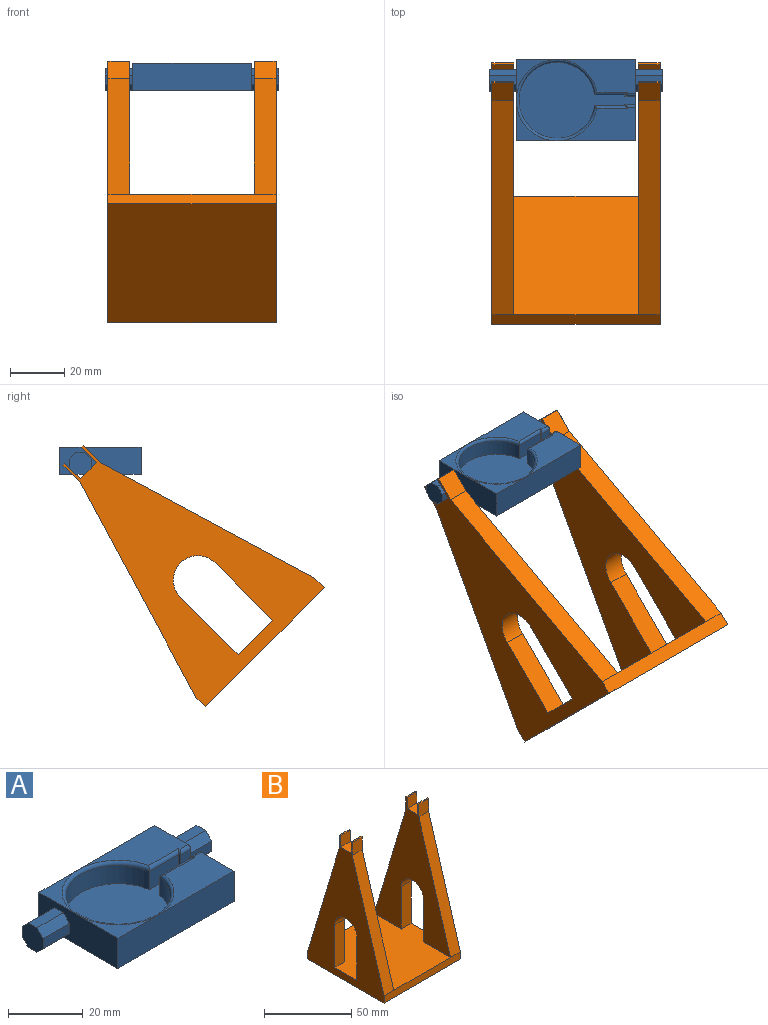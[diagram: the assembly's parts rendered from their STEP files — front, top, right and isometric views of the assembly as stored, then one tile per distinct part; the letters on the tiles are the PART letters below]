
ASSEMBLY  parts=2 mates=1
PART A: 40 faces, bbox 64x34x10 mm
  f0: plane 29x12.41mm, normal (0,0,1), area 217.2mm2, adj f3,f7,f33,f34,f35,f36
  f1: plane 29x12.59mm, normal (0,0,1), area 217.7mm2, adj f3,f6,f36,f37,f38,f39
  f2: plane 15x15mm, normal (0,0,1), area 48.3mm2, adj f4,f7,f36
  f3: plane 30x10mm, normal (1,0,0), area 225.6mm2, adj f0,f1,f6,f7,f8,f12,f13,f16
  f4: plane 30x10mm, normal (-1,0,0), area 247mm2, adj f2,f5,f6,f7,f8,f17,f18,f19
  f5: plane 15x15mm, normal (0,0,1), area 48.3mm2, adj f4,f6,f36
  f6: plane 44x10mm, normal (0,1,0), area 440mm2, adj f1,f3,f4,f5,f8
  f7: plane 44x10mm, normal (0,-1,0), area 440mm2, adj f0,f2,f3,f4,f8
  f8: plane 64x30mm, normal (0,0,-1), area 1386.3mm2, adj f3,f4,f6,f7,f17,f23,f24,f25
  f9: cylinder r=14mm len=28mm, axis (0,0,1), area 503.7mm2, adj f10,f15,f16,f36
  f10: plane 11.14x6mm, normal (0,1,0), area 66.9mm2, adj f9,f11,f16,f35
  f11: plane 6x0.41mm, normal (-1,0,0), area 2.5mm2, adj f10,f12,f16,f34
  f12: plane 6x4mm, normal (0,1,0), area 24mm2, adj f3,f11,f16,f33
  f13: plane 6x4mm, normal (0,-1,0), area 24mm2, adj f3,f14,f16,f38
  f14: plane 6x0.59mm, normal (-1,0,0), area 3.5mm2, adj f13,f15,f16,f39
  f15: plane 11.14x6mm, normal (0,-1,0), area 66.9mm2, adj f9,f14,f16,f37
  f16: plane 43x28mm, normal (0,0,1), area 671.9mm2, adj f3,f9,f10,f11,f12,f13,f14,f15
  f17: plane 10x2.34mm, normal (0,-0.71,-0.71), area 33.1mm2, adj f4,f8,f18,f24
  f18: plane 10x3.31mm, normal (0,-1,0), area 33.1mm2, adj f4,f17,f19,f24
  f19: plane 10x2.34mm, normal (0,-0.71,0.71), area 33.1mm2, adj f4,f18,f20,f24
  f20: plane 10x3.31mm, normal (0,0,1), area 33.1mm2, adj f4,f19,f21,f24
  f21: plane 10x2.34mm, normal (0,0.71,0.71), area 33.1mm2, adj f4,f20,f22,f24
  f22: plane 10x3.31mm, normal (0,1,0), area 33.1mm2, adj f4,f21,f23,f24
  f23: plane 10x2.34mm, normal (0,0.71,-0.71), area 33.1mm2, adj f4,f8,f22,f24
  f24: plane 8x8mm, normal (-1,0,0), area 53mm2, adj f8,f17,f18,f19,f20,f21,f22,f23
  f25: plane 10x2.34mm, normal (0,0.71,-0.71), area 33.1mm2, adj f3,f8,f26,f32
  f26: plane 10x3.31mm, normal (0,1,0), area 33.1mm2, adj f3,f25,f27,f32
  f27: plane 10x2.34mm, normal (0,0.71,0.71), area 33.1mm2, adj f3,f26,f28,f32
  f28: plane 10x3.31mm, normal (0,0,1), area 33.1mm2, adj f3,f27,f29,f32
  f29: plane 10x2.34mm, normal (0,-0.71,0.71), area 33.1mm2, adj f3,f28,f30,f32
  f30: plane 10x3.31mm, normal (0,-1,0), area 33.1mm2, adj f3,f29,f31,f32
  f31: plane 10x2.34mm, normal (0,-0.71,-0.71), area 33.1mm2, adj f3,f8,f30,f32
  f32: plane 8x8mm, normal (1,0,0), area 53mm2, adj f8,f25,f26,f27,f28,f29,f30,f31
  f33: cylinder r=1mm len=4mm, axis (-1,0,0), area 5.7mm2, adj f0,f3,f12,f34
  f34: cylinder r=1mm len=1.41mm, axis (0,-1,0), area 0.6mm2, adj f0,f11,f33,f35
  f35: cylinder r=1mm len=12.14mm, axis (-1,0,0), area 17.6mm2, adj f0,f10,f34,f36
  f36: torus R=15mm, axis (0,0,1), area 134.3mm2, adj f0,f1,f2,f5,f9,f35,f37
  f37: cylinder r=1mm len=12.14mm, axis (1,0,0), area 17.6mm2, adj f1,f15,f36,f39
  f38: cylinder r=1mm len=4mm, axis (1,0,0), area 5.7mm2, adj f1,f3,f13,f39
  f39: cylinder r=1mm len=1.59mm, axis (0,-1,0), area 0.9mm2, adj f1,f14,f37,f38
PART B: 32 faces, bbox 62x62x100 mm
  f0: plane 8x1mm, normal (0,0,1), area 8mm2, adj f4,f6,f29,f30
  f1: plane 8x1mm, normal (0,0,1), area 8mm2, adj f4,f6,f23,f27
  f2: plane 8x1mm, normal (0,0,1), area 8mm2, adj f5,f7,f17,f21
  f3: plane 8x1mm, normal (0,0,1), area 8mm2, adj f5,f7,f12,f19
  f4: plane 100x62mm, normal (1,0,0), area 2786.8mm2, adj f0,f1,f8,f9,f10,f11,f22,f23
  f5: plane 100x62mm, normal (-1,0,0), area 2786.8mm2, adj f2,f3,f8,f9,f10,f11,f12,f13
  f6: plane 95x62mm, normal (-1,0,0), area 2476.8mm2, adj f0,f1,f8,f22,f23,f24,f25,f26
  f7: plane 95x62mm, normal (1,0,0), area 2476.8mm2, adj f2,f3,f8,f12,f13,f14,f15,f16
  f8: plane 62x62mm, normal (0,0,1), area 3140mm2, adj f4,f5,f6,f7,f9,f10,f14,f15
  f9: plane 62x5mm, normal (0,-1,0), area 310mm2, adj f4,f5,f8,f11,f13,f22
  f10: plane 62x5mm, normal (0,1,0), area 310mm2, adj f4,f5,f8,f11,f20,f31
  f11: plane 62x62mm, normal (0,0,-1), area 3844mm2, adj f4,f5,f9,f10
  f12: plane 9x8mm, normal (0,-1,0), area 72mm2, adj f3,f5,f7,f13
  f13: plane 86x25.75mm, normal (0,-0.96,0.29), area 718.2mm2, adj f5,f7,f9,f12
  f14: plane 30x8mm, normal (0,1,0), area 240mm2, adj f5,f7,f8,f16
  f15: plane 30x8mm, normal (0,-1,0), area 240mm2, adj f5,f7,f8,f16
  f16: cylinder r=9mm len=18mm, axis (1,0,0), area 226.2mm2, adj f5,f7,f14,f15
  f17: plane 8x8mm, normal (0,-1,0), area 64mm2, adj f2,f5,f7,f18
  f18: plane 8.5x8mm, normal (0,0,1), area 68mm2, adj f5,f7,f17,f19
  f19: plane 8x8mm, normal (0,1,0), area 64mm2, adj f3,f5,f7,f18
  f20: plane 86x25.75mm, normal (0,0.96,0.29), area 718.2mm2, adj f5,f7,f10,f21
  f21: plane 9x8mm, normal (0,1,0), area 72mm2, adj f2,f5,f7,f20
  f22: plane 86x25.75mm, normal (0,-0.96,0.29), area 718.2mm2, adj f4,f6,f9,f23
  f23: plane 9x8mm, normal (0,-1,0), area 72mm2, adj f1,f4,f6,f22
  f24: cylinder r=9mm len=18mm, axis (1,0,0), area 226.2mm2, adj f4,f6,f25,f26
  f25: plane 30x8mm, normal (0,1,0), area 240mm2, adj f4,f6,f8,f24
  f26: plane 30x8mm, normal (0,-1,0), area 240mm2, adj f4,f6,f8,f24
  f27: plane 8x8mm, normal (0,1,0), area 64mm2, adj f1,f4,f6,f28
  f28: plane 8.5x8mm, normal (0,0,1), area 68mm2, adj f4,f6,f27,f29
  f29: plane 8x8mm, normal (0,-1,0), area 64mm2, adj f0,f4,f6,f28
  f30: plane 9x8mm, normal (0,1,0), area 72mm2, adj f0,f4,f6,f31
  f31: plane 86x25.75mm, normal (0,0.96,0.29), area 718.2mm2, adj f4,f6,f10,f30
PLACE A t=(23.66,48.02,50.48)mm
PLACE B rot(axis=(-1,0,0),45deg) t=(30.66,-12.62,-23.23)mm
MATE fastened B.f29 <-> A.f25  axis (0,-0.71,0.71) through (57.66,58.26,41.65)mm
